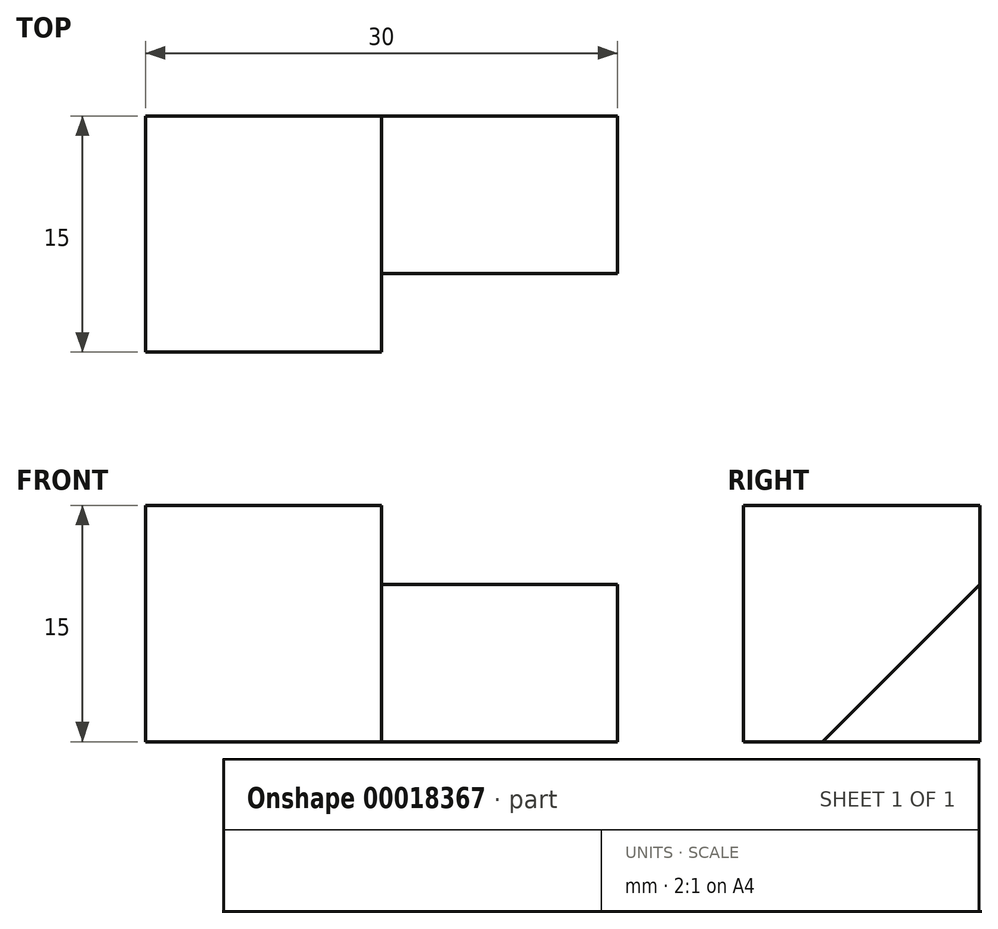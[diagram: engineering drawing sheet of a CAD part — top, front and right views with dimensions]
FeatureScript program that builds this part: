
annotation { "Feature Type Name" : "Feature", "Feature Type Description" : "" }
export const myFeature = defineFeature(function(context is Context, id is Id, definition is map)
    precondition{}
    {
        {
            var Q0;
            Q0=qCreatedBy(makeId("Right.planeOp"),FACE);
            var sketch = newSketch(context, id + "F0", { "sketchPlane" : qUnion([Q0])});
            skLineSegment(sketch, "E0", {"start": v(-34.21, 35.99) * mm, "end": v(-34.21, 20.99) * mm});
            skLineSegment(sketch, "E1", {"start": v(-34.21, 20.99) * mm, "end": v(-19.21, 20.99) * mm});
            skLineSegment(sketch, "E2", {"start": v(-19.21, 20.99) * mm, "end": v(-19.21, 35.99) * mm});
            skLineSegment(sketch, "E3", {"start": v(-19.21, 35.99) * mm, "end": v(-34.21, 35.99) * mm});
            skSolve(sketch);
        }
        {
            var Q0;
            Q0=makeQuery(id+"F0.imprint","IMPRINT",FACE,{"disambiguationData":[TD([[makeQuery(id+"F0.imprint","IMPRINT",EDGE,{"derivedFrom":sQuery(id+"F0.wireOp",EDGE,"E0")}),1.0]])]});
            extrude(context, id + "F1", {"entities" : qUnion([Q0]), "depth" : 15 * mm});
        }
        {
            var Q0;
            Q0=makeQuery(id+"F1.opExtrude","CAP_FACE",FACE,{"disambiguationData":[OSD([sQuery(id+"F0.wireOp",EDGE,"E0"),sQuery(id+"F0.wireOp",EDGE,"E1"),sQuery(id+"F0.wireOp",EDGE,"E2"),sQuery(id+"F0.wireOp",EDGE,"E3")])],"isStart":false});
            var sketch = newSketch(context, id + "F2", { "sketchPlane" : qUnion([Q0])});
            skLineSegment(sketch, "E4", {"start": v(-19.21, 30.99) * mm, "end": v(-29.21, 20.99) * mm});
            skLineSegment(sketch, "E5", {"start": v(-29.21, 20.99) * mm, "end": v(-19.21, 20.99) * mm});
            skLineSegment(sketch, "E6", {"start": v(-19.21, 20.99) * mm, "end": v(-19.21, 30.99) * mm});
            skSolve(sketch);
        }
        {
            var Q0;
            Q0=makeQuery(id+"F2.imprint","IMPRINT",FACE,{"disambiguationData":[TD([[makeQuery(id+"F2.imprint","IMPRINT",EDGE,{"derivedFrom":sQuery(id+"F2.wireOp",EDGE,"E4")}),1.0]])]});
            extrude(context, id + "F3", {"entities" : qUnion([Q0]), "operationType" : NewBodyOperationType.ADD, "depth" : 15 * mm});
        }
    });
